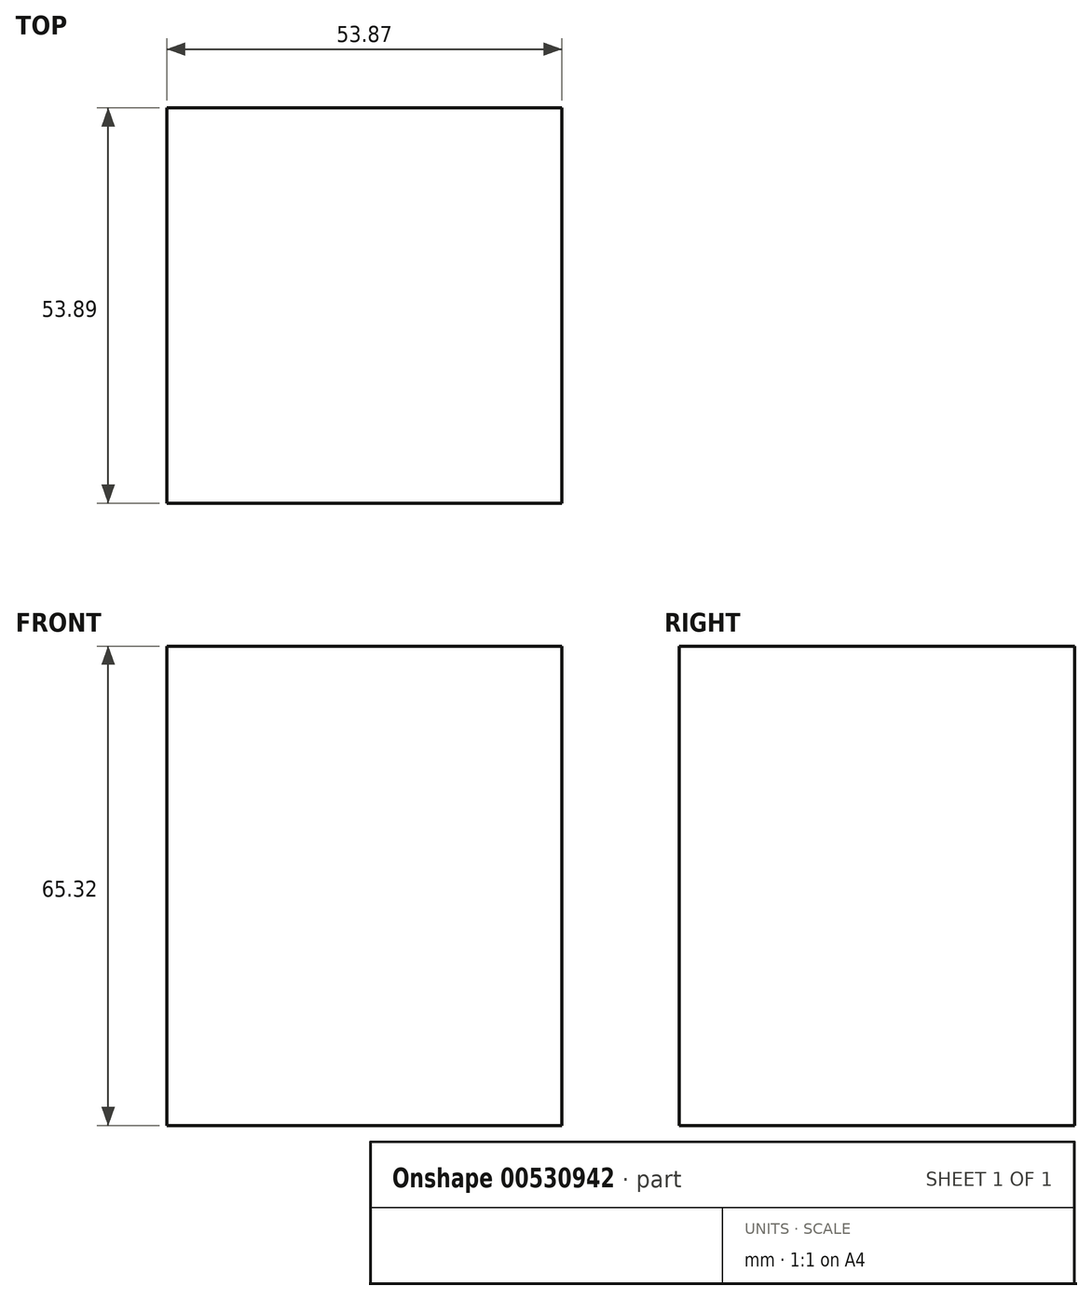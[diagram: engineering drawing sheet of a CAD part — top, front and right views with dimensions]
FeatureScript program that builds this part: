
annotation { "Feature Type Name" : "Feature", "Feature Type Description" : "" }
export const myFeature = defineFeature(function(context is Context, id is Id, definition is map)
    precondition{}
    {
        {
            var Q0;
            Q0=qCreatedBy(makeId("Top.planeOp"),FACE);
            var sketch = newSketch(context, id + "F0", { "sketchPlane" : qUnion([Q0])});
            skLineSegment(sketch, "E0.bottom", {"start": v(0, 21.7) * mm, "end": v(-53.87, 21.7) * mm});
            skLineSegment(sketch, "E0.top", {"start": v(0, 75.58) * mm, "end": v(-53.87, 75.58) * mm});
            skLineSegment(sketch, "E0.left", {"start": v(0, 21.7) * mm, "end": v(0, 75.58) * mm});
            skLineSegment(sketch, "E0.right", {"start": v(-53.87, 21.7) * mm, "end": v(-53.87, 75.58) * mm});
            skSolve(sketch);
        }
        {
            var Q0;
            Q0=makeQuery(id+"F0.imprint","IMPRINT",FACE,{"disambiguationData":[TD([[makeQuery(id+"F0.imprint","IMPRINT",EDGE,{"derivedFrom":sQuery(id+"F0.wireOp",EDGE,"E0.bottom")}),-1.0]])]});
            extrude(context, id + "F1", {"entities" : qUnion([Q0]), "depth" : 65.32 * mm, "offsetDistance" : 25.4 * mm});
        }
    });
